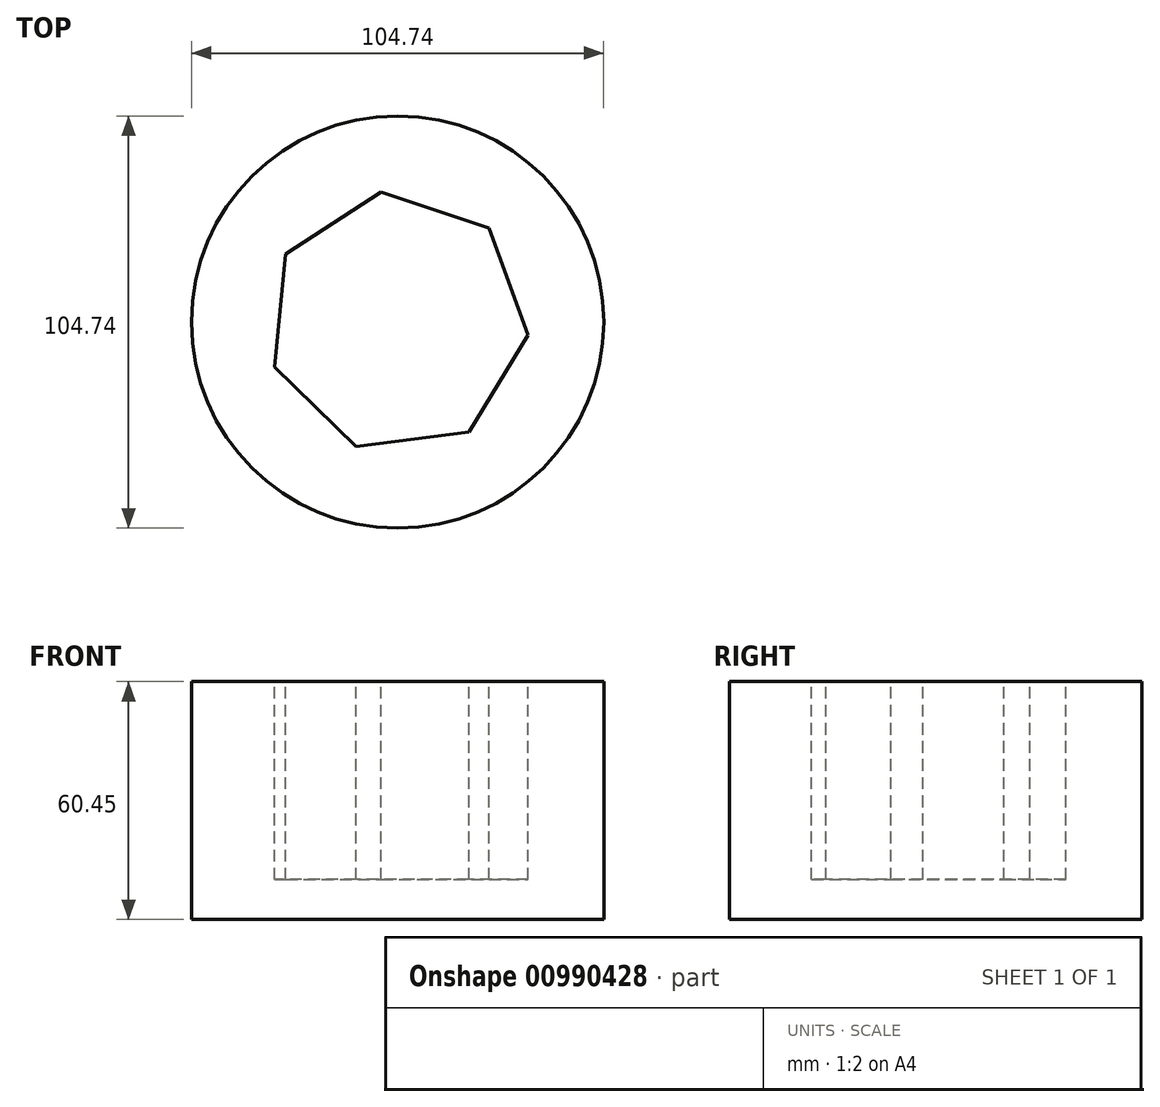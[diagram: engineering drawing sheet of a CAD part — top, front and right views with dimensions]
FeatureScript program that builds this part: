
annotation { "Feature Type Name" : "Feature", "Feature Type Description" : "" }
export const myFeature = defineFeature(function(context is Context, id is Id, definition is map)
    precondition{}
    {
        {
            var Q0;
            Q0=qCreatedBy(makeId("Top.planeOp"),FACE);
            var sketch = newSketch(context, id + "F0", { "sketchPlane" : qUnion([Q0])});
            skCircle(sketch, "E0", {"center": v(0, 0) * mm, "radius": 52.37 * mm});
            skSolve(sketch);
        }
        {
            var Q0;
            Q0=makeQuery(id+"F0.imprint","IMPRINT",FACE,{"disambiguationData":[TD([[makeQuery(id+"F0.imprint","IMPRINT",EDGE,{"derivedFrom":sQuery(id+"F0.wireOp",EDGE,"E0")}),1.0]])]});
            extrude(context, id + "F1", {"entities" : qUnion([Q0]), "depth" : 60.45 * mm, "offsetDistance" : 25.4 * mm});
        }
        {
            var Q0;
            Q0=makeQuery(id+"F1.opExtrude","CAP_FACE",FACE,{"disambiguationData":[OSD([sQuery(id+"F0.wireOp",EDGE,"E0")])],"isStart":false});
            var sketch = newSketch(context, id + "F2", { "sketchPlane" : qUnion([Q0])});
            skCircle(sketch, "E1.cCircle", {"center": v(0, 0) * mm, "radius": 30.02 * mm, "construction": true});
            skLineSegment(sketch, "E1.0", {"start": v(-28.46, 17.32) * mm, "end": v(-4.2, 33.05) * mm});
            skLineSegment(sketch, "E1.1", {"start": v(-4.2, 33.05) * mm, "end": v(23.22, 23.9) * mm});
            skLineSegment(sketch, "E1.2", {"start": v(23.22, 23.9) * mm, "end": v(33.16, -3.26) * mm});
            skLineSegment(sketch, "E1.3", {"start": v(33.16, -3.26) * mm, "end": v(18.13, -27.95) * mm});
            skLineSegment(sketch, "E1.4", {"start": v(18.13, -27.95) * mm, "end": v(-10.55, -31.6) * mm});
            skLineSegment(sketch, "E1.5", {"start": v(-10.55, -31.6) * mm, "end": v(-31.29, -11.45) * mm});
            skLineSegment(sketch, "E1.6", {"start": v(-31.29, -11.45) * mm, "end": v(-28.46, 17.32) * mm});
            skPoint(sketch, "E1.0.midPoint", {"position": v(-16.33, 25.18) * mm});
            skSolve(sketch);
        }
        {
            var Q0;
            Q0=makeQuery(id+"F2.imprint","IMPRINT",FACE,{"disambiguationData":[TD([[makeQuery(id+"F2.imprint","IMPRINT",EDGE,{"derivedFrom":sQuery(id+"F2.wireOp",EDGE,"E1.0")}),-1.0]])]});
            extrude(context, id + "F3", {"entities" : qUnion([Q0]), "operationType" : NewBodyOperationType.REMOVE, "oppositeDirection" : true, "depth" : 50.3 * mm, "offsetDistance" : 25.4 * mm});
        }
    });
